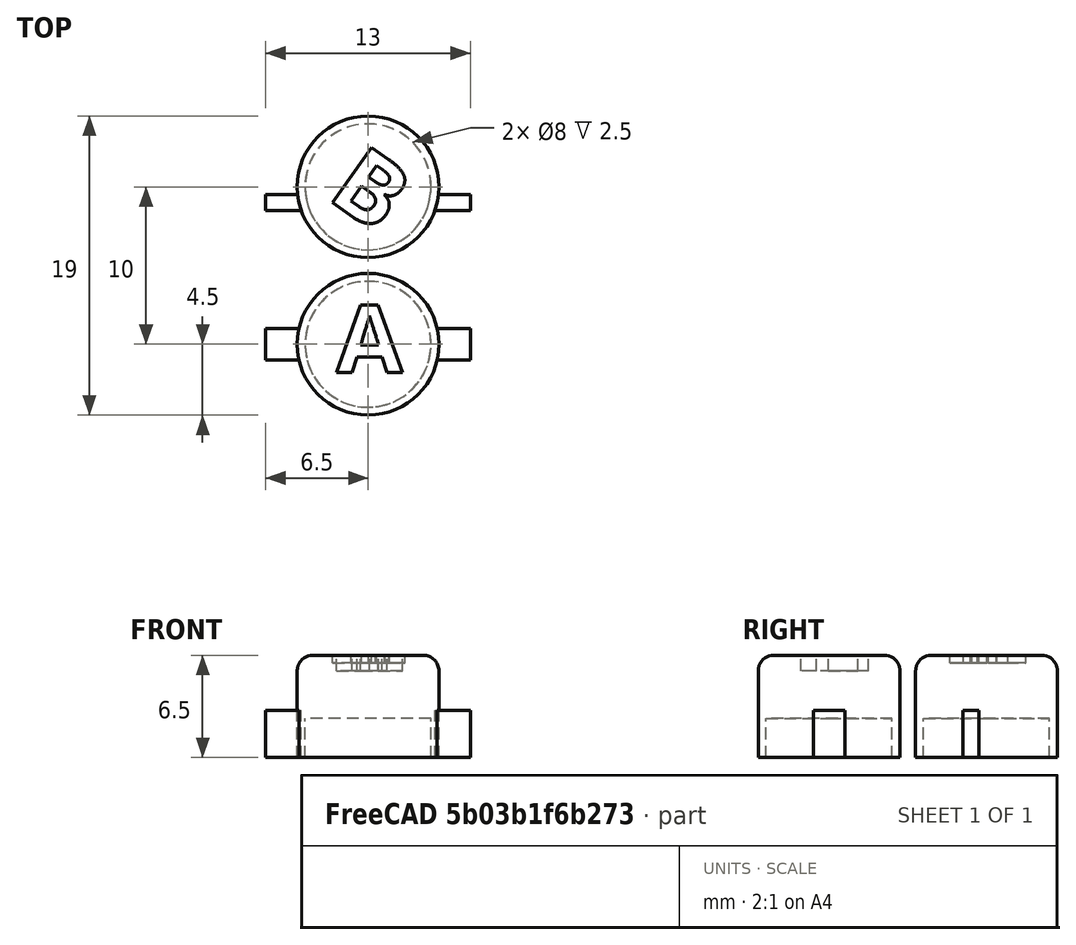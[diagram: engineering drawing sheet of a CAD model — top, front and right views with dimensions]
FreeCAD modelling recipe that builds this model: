
FCSTD DOCUMENT  (FreeCAD 0.18R16131 (Git))
Label: GBC_A_B_soft
License: All rights reserved
LicenseURL: http://en.wikipedia.org/wiki/All_rights_reserved
objects: Part::Cylinder×4, Part::Cut×4, Part::Box×2, Part::Fillet×2, Part::Part2DObjectPython×2, Part::Extrusion×2, Part::MultiFuse×2
note: 18 computed .brp shape members not serialized (recipe doc carries the construction recipe); baked Part::Feature solids carry a one-line shape summary decoded from their .brp

FEATURE [Part::Cylinder] Cylinder
  Angle = 360
  AttacherType = Attacher::AttachEngine3D
  Height = 6.5
  Radius = 4.5
FEATURE [Part::Box] Box  label="Cube"
  AttacherType = Attacher::AttachEngine3D
  Height = 3
  Length = 13
  Placement = pos=(-6.5,-1,0) rot=(0,0,1;0rad)
  Width = 2
FEATURE [Part::Fillet] Fillet
  Base = -> Cylinder
  Edges = 1 edges r=1: [Edge1]
FEATURE [Part::Part2DObjectPython] ShapeString  # Draft 2D object (typed FeaturePython)
  FontFile = <userpath>/A6E4-ED97/3dprinting/fonts/open-sans/OpenSans-Bold.ttf
  Placement = pos=(-2,-2,7) rot=(0,0,1;0rad)
  Size = 5.5
  String = A
  Tracking = 0
FEATURE [Part::Part2DObjectPython] ShapeString001  # Draft 2D object (typed FeaturePython)
  FontFile = <userpath>/A6E4-ED97/3dprinting/fonts/open-sans/OpenSans-Bold.ttf
  Placement = pos=(-2.7,9.3,7) rot=(0,0,-1;0.610865rad)
  Size = 5.5
  String = B
  Tracking = 0
FEATURE [Part::Extrusion] Extrude
  Base = -> ShapeString
  Dir = (0,0,1)
  DirMode = 2
  FaceMakerClass = Part::FaceMakerBullseye
  LengthFwd = 1
  LengthRev = 0
  Placement = pos=(0,0.2,-1.5) rot=(0,0,1;0rad)
  Solid = false
  Symmetric = false
FEATURE [Part::Cylinder] Cylinder001
  Angle = 360
  AttacherType = Attacher::AttachEngine3D
  Height = 6.5
  Placement = pos=(0,10,0) rot=(0,0,1;0rad)
  Radius = 4.5
FEATURE [Part::Fillet] Fillet001
  Base = -> Cylinder001
  Edges = 1 edges r=1: [Edge1]
FEATURE [Part::Box] Box001  label="Cube001"
  AttacherType = Attacher::AttachEngine3D
  Height = 3
  Length = 13
  Placement = pos=(-6.5,8.5,0) rot=(0,0,1;0rad)
  Width = 1
FEATURE [Part::Extrusion] Extrude001
  Base = -> ShapeString001
  Dir = (0,0,1)
  DirMode = 2
  FaceMakerClass = Part::FaceMakerBullseye
  LengthFwd = 1
  LengthRev = 0
  Placement = pos=(0,0,-1) rot=(0,0,1;0rad)
  Solid = false
  Symmetric = false
FEATURE [Part::Cut] Cut
  Base = -> Fillet001
  Tool = -> Extrude001
FEATURE [Part::Cut] Cut001
  Base = -> Fillet
  Tool = -> Extrude
FEATURE [Part::Cylinder] Cylinder002
  Angle = 360
  AttacherType = Attacher::AttachEngine3D
  Height = 2.5
  Radius = 4
FEATURE [Part::MultiFuse] Fusion
  Shapes = -> [Cut001,Box]
FEATURE [Part::Cut] Cut002
  Base = -> Fusion
  Tool = -> Cylinder002
FEATURE [Part::Cylinder] Cylinder003
  Angle = 360
  AttacherType = Attacher::AttachEngine3D
  Height = 2.5
  Placement = pos=(0,10,0) rot=(0,0,1;0rad)
  Radius = 4
FEATURE [Part::MultiFuse] Fusion001
  Shapes = -> [Cut,Box001]
FEATURE [Part::Cut] Cut003
  Base = -> Fusion001
  Tool = -> Cylinder003
